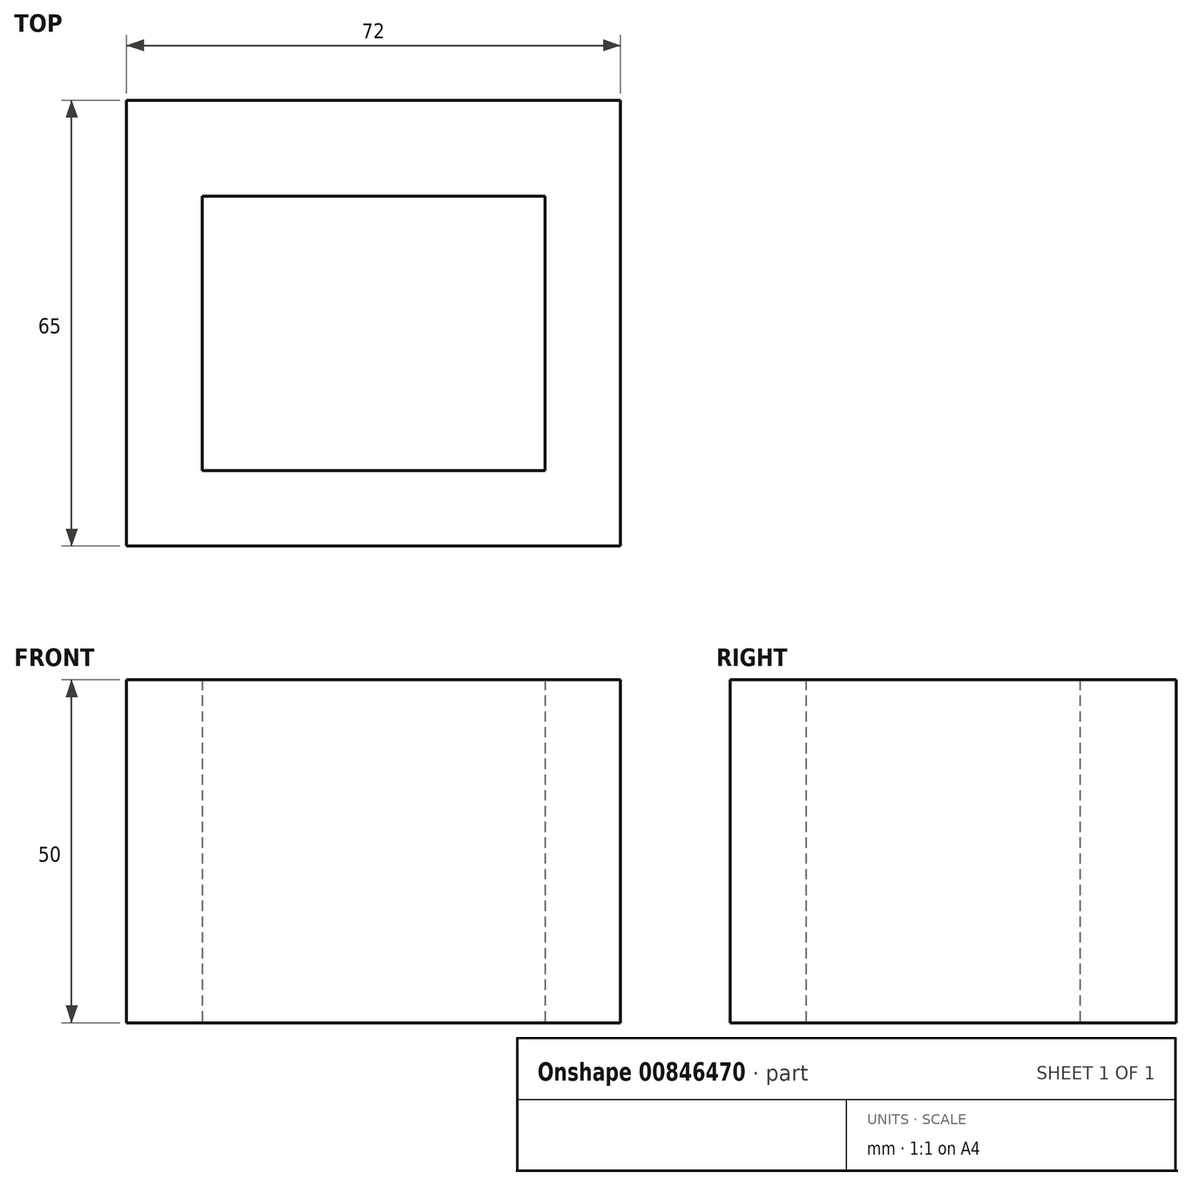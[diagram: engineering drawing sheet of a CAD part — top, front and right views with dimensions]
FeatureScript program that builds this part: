
annotation { "Feature Type Name" : "Feature", "Feature Type Description" : "" }
export const myFeature = defineFeature(function(context is Context, id is Id, definition is map)
    precondition{}
    {
        {
            var Q0;
            Q0=qCreatedBy(makeId("Top.planeOp"),FACE);
            var sketch = newSketch(context, id + "F0", { "sketchPlane" : qUnion([Q0])});
            skLineSegment(sketch, "E0.bottom", {"start": v(36, -32.5) * mm, "end": v(-36, -32.5) * mm});
            skLineSegment(sketch, "E0.top", {"start": v(36, 32.5) * mm, "end": v(-36, 32.5) * mm});
            skLineSegment(sketch, "E0.left", {"start": v(36, -32.5) * mm, "end": v(36, 32.5) * mm});
            skLineSegment(sketch, "E0.right", {"start": v(-36, -32.5) * mm, "end": v(-36, 32.5) * mm});
            skPoint(sketch, "E0.middle", {"position": v(0, 0) * mm});
            skLineSegment(sketch, "E1.bottom", {"start": v(-25, -21.5) * mm, "end": v(25, -21.5) * mm});
            skLineSegment(sketch, "E1.top", {"start": v(-25, 18.5) * mm, "end": v(25, 18.5) * mm});
            skLineSegment(sketch, "E1.left", {"start": v(-25, -21.5) * mm, "end": v(-25, 18.5) * mm});
            skLineSegment(sketch, "E1.right", {"start": v(25, -21.5) * mm, "end": v(25, 18.5) * mm});
            skSolve(sketch);
        }
        {
            var Q0;
            Q0=makeQuery(id+"F0.imprint","IMPRINT",FACE,{"disambiguationData":[TD([[makeQuery(id+"F0.imprint","IMPRINT",EDGE,{"derivedFrom":sQuery(id+"F0.wireOp",EDGE,"E0.bottom")}),-1.0]])]});
            extrude(context, id + "F1", {"entities" : qUnion([Q0]), "depth" : 50 * mm, "offsetDistance" : 25 * mm});
        }
    });
